# Revit family: Vitra_Arkitekt_UrinalDivision_5172L003-0155
name_source: partatom
category: Plumbing Fixtures
revit_build: Autodesk Revit 2017 (Build: 20160225_1515(x64)
units: mm (PartAtom-declared; Revit-internal decimal feet)

## family parameters
Cut with Voids When Loaded = No
Host = Face
OmniClass Number = 23.45.05.21.11.21
OmniClass Title = Urinals
Part Type = Normal
Room Calculation Point = No
Round Connector Dimension = Use Diameter
Shared = Yes

## types (1)
- UrinalDivision_Vitra_Arkitekt_5172L003-0155
    Article No. (default) = 5172L003-0155
    BIMobject category = Sanitary - Screens & Dividers
    CW Connection = No
    Color = White
    Cost = 0 $
    Default Elevation = 650 mm  [stored 2.13255 ft]
    Description = VitrA Arkitekt Urinal Division
    Design country = Turkey
    HW Connection = No
    IFC Classification = Sanitary Terminal
    Main Material = Ceramic
    Manufacturer = Vitra
    Manufacturer name = Vitra
    Masterformat 2014 Code = 22 41 13.16
    Masterformat 2014 Description = Residential Urinals
    Model = 5172L003-0155
    MountingType = Wall Mounted
    NBS Referans Code = 31-93
    NBS Referans Description = Urinal And Wc Fittings
    Nominal Depth = 400 mm  [stored 1.31234 ft]
    NominalHeight = 600 mm
    NominalWidth = 100 mm  [stored 0.328084 ft]
    OmniClass Code = 23-15 11 15 11
    OmniClass Description = Toilet Compartments and Urinal Screens
    Product SKU = 5172L003-0155
    Product certification = https://vitraglobal.com
    Product data url = https://www.vitra.com.tr
    Product family = Wall Mounted Urinal Division
    Product group = Arkitekt
    Secondary Material = Vitra-Ceramic-White
    Technical description = https://www.vitra.com.tr
    UNSPSC Code = 30181508
    UNSPSC Description = Restroom partitions
    URL = https://www.vitra.com.tr
    Uniclass 1.4 Code = L385
    Uniclass 1.4 Description = Room dividers, screens
    Uniclass 2.0 Code = PR-31-93
    Uniclass 2.0 Description = Urinal And Wc Fittings
    Uniclass 2015 Code = Pr_40_20_93
    Uniclass 2015 Name = Urinal and WC fittings
    Uniformat II Code = E2010
    Uniformat II Description = Fixed Furnishings
    Vent Connection = No
    Warranty Period (Year) = 10 Years
    Waste Connection = No
    Weight Net (kg) = 11,340
    Youtube = https://www.youtube.com

note: [stored X ft] marks values corroborated as IEEE doubles in the binary element streams (Revit-internal decimal feet)

## geometry (parser evidence)
native form markers: Sweep x3
no freeform markers — native parametric forms only
